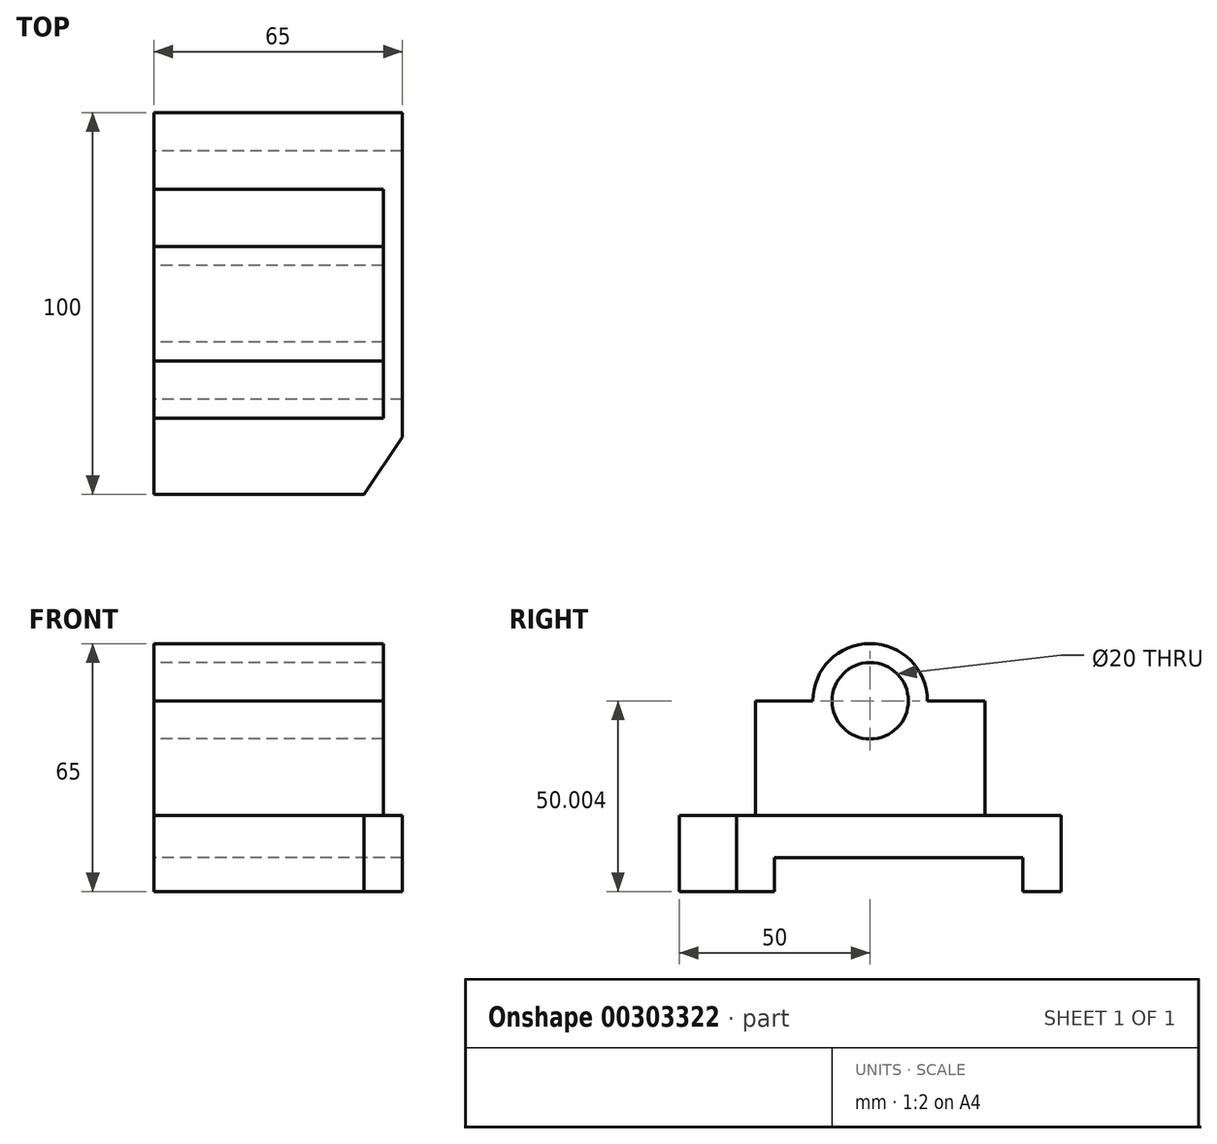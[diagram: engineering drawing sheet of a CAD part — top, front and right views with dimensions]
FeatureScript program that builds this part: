
annotation { "Feature Type Name" : "Feature", "Feature Type Description" : "" }
export const myFeature = defineFeature(function(context is Context, id is Id, definition is map)
    precondition{}
    {
        {
            var Q0;
            Q0=qCreatedBy(makeId("Right.planeOp"),FACE);
            var sketch = newSketch(context, id + "F0", { "sketchPlane" : qUnion([Q0])});
            skLineSegment(sketch, "E0.bottom", {"start": v(-50, -32.37) * mm, "end": v(50, -32.37) * mm});
            skLineSegment(sketch, "E0.top", {"start": v(-50, -52.37) * mm, "end": v(50, -52.37) * mm});
            skLineSegment(sketch, "E0.left", {"start": v(-50, -32.37) * mm, "end": v(-50, -52.37) * mm});
            skLineSegment(sketch, "E0.right", {"start": v(50, -32.37) * mm, "end": v(50, -52.37) * mm});
            skLineSegment(sketch, "E1.bottom", {"start": v(-30, -2.37) * mm, "end": v(30, -2.37) * mm});
            skLineSegment(sketch, "E1.top", {"start": v(-30, -32.37) * mm, "end": v(30, -32.37) * mm});
            skLineSegment(sketch, "E1.left", {"start": v(-30, -2.37) * mm, "end": v(-30, -32.37) * mm});
            skLineSegment(sketch, "E1.right", {"start": v(30, -2.37) * mm, "end": v(30, -32.37) * mm});
            skCircle(sketch, "E2", {"center": v(0, -2.37) * mm, "radius": 15 * mm});
            skCircle(sketch, "E3", {"center": v(0, -2.37) * mm, "radius": 10 * mm});
            skLineSegment(sketch, "E4.bottom", {"start": v(-25, -52.37) * mm, "end": v(40, -52.37) * mm});
            skLineSegment(sketch, "E4.top", {"start": v(-25, -43.41) * mm, "end": v(40, -43.41) * mm});
            skLineSegment(sketch, "E4.left", {"start": v(-25, -52.37) * mm, "end": v(-25, -43.41) * mm});
            skLineSegment(sketch, "E4.right", {"start": v(40, -52.37) * mm, "end": v(40, -43.41) * mm});
            skSolve(sketch);
        }
        {
            var Q0;
            {var subQ4=sQuery(id+"F0.wireOp",EDGE,"E0.left");Q0=makeQuery(id+"F0.imprint","IMPRINT",FACE,{"disambiguationData":[TD([[makeQuery(id+"F0.imprint","IMPRINT",EDGE,{"derivedFrom":subQ4}),1.0]])]});}
            extrude(context, id + "F1", {"entities" : qUnion([Q0]), "depth" : 65 * mm});
        }
        {
            var Q0;
            Q0 = qSketchRegion(id + "F0", true);
            extrude(context, id + "F2", {"entities" : qUnion([Q0]), "operationType" : NewBodyOperationType.ADD, "depth" : 60 * mm});
        }
        {
            var Q0;
            {var subQ0=sQuery(id+"F0.wireOp",EDGE,"E0.right");var subQ1=sQuery(id+"F0.wireOp",EDGE,"E0.top");var subQ3=sQuery(id+"F0.wireOp",EDGE,"E4.bottom");var subQ5=sQuery(id+"F0.wireOp",EDGE,"E0.left");Q0=makeQuery(id+"F2.boolean.opBoolean","SPLIT",FACE,{"disambiguationData":[TD([makeQuery(id+"F1.opExtrude","SWEPT_FACE",FACE,{"disambiguationData":[OSD([sQuery(id+"F0.wireOp",EDGE,"E4.top")])]})])],"derivedFrom":makeQuery(id+"F2.opExtrude","CAP_FACE",FACE,{"disambiguationData":[OSD([sQuery(id+"F0.wireOp",EDGE,"E0.bottom"),subQ1,subQ5,subQ0,sQuery(id+"F0.wireOp",EDGE,"E1.bottom"),sQuery(id+"F0.wireOp",EDGE,"E1.left"),sQuery(id+"F0.wireOp",EDGE,"E1.right"),sQuery(id+"F0.wireOp",EDGE,"E2"),sQuery(id+"F0.wireOp",EDGE,"E3"),subQ3])],"isStart":false})});}
            var sketch = newSketch(context, id + "F3", { "sketchPlane" : qUnion([Q0])});
            skSolve(sketch);
        }
        {
            var Q0;
            Q0 = qSketchRegion(id + "F3", true);
            var Q1;
            {var subQ0=sQuery(id+"F0.wireOp",EDGE,"E4.bottom");var subQ1=sQuery(id+"F0.wireOp",EDGE,"E0.top");Q1=makeQuery(id+"F3.imprint","IMPRINT",FACE,{"disambiguationData":[TD([[makeQuery(id+"F3.imprint","IMPRINT",EDGE,{"derivedFrom":makeQuery(id+"F2.opExtrude","CAP_EDGE",EDGE,{"disambiguationData":[OSD([subQ1,subQ0])],"isStart":false})}),1.0]])]});}
            extrude(context, id + "F4", {"entities" : qUnion([Q0, Q1]), "operationType" : NewBodyOperationType.REMOVE, "oppositeDirection" : true, "depth" : 100 * mm});
        }
        {
            var Q0;
            Q0=makeQuery(id+"F1.opExtrude","SWEPT_FACE",FACE,{"disambiguationData":[OSD([sQuery(id+"F0.wireOp",EDGE,"E0.bottom"),sQuery(id+"F0.wireOp",EDGE,"E1.top")])]});
            var sketch = newSketch(context, id + "F5", { "sketchPlane" : qUnion([Q0])});
            skLineSegment(sketch, "E5", {"start": v(55, -50) * mm, "end": v(65, -35) * mm});
            skSolve(sketch);
        }
        {
            var Q0;
            Q0 = qSketchRegion(id + "F5", true);
            var Q1;
            {var subQ0=sQuery(id+"F5.wireOp",EDGE,"E5");Q1=makeQuery(id+"F5.imprint","IMPRINT",FACE,{"disambiguationData":[TD([[makeQuery(id+"F5.imprint","IMPRINT",EDGE,{"derivedFrom":subQ0}),-1.0]])]});}
            extrude(context, id + "F6", {"entities" : qUnion([Q0, Q1]), "operationType" : NewBodyOperationType.REMOVE, "oppositeDirection" : true, "depth" : 25 * mm});
        }
    });
